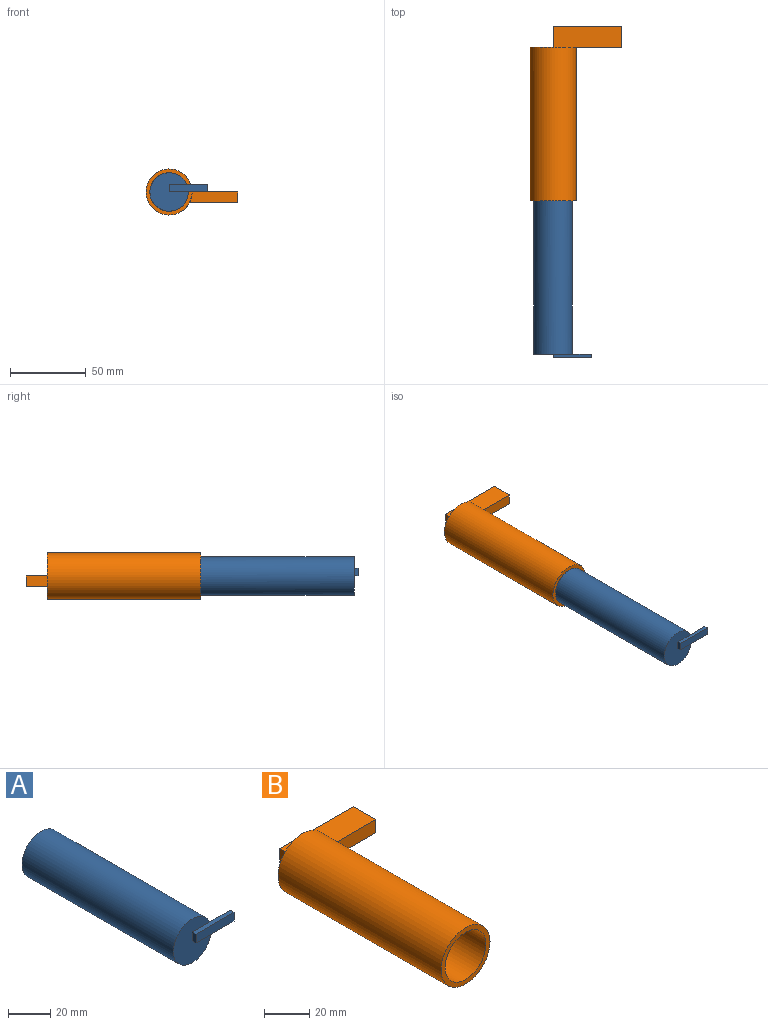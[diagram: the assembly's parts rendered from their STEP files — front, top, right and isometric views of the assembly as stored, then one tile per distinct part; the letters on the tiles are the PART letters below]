
ASSEMBLY  parts=2 mates=1
PART A: 9 faces, bbox 38.1x104.1x25.4 mm
  f0: plane 25.4x25.4mm, normal (0,-1,0), area 444mm2, adj f1,f4,f5,f6
  f1: cylinder r=12.7mm len=101.6mm, axis (0,1,0), area 8107.3mm2, adj f0,f2,f3
  f2: plane 25.4x25.4mm, normal (0,1,0), area 506.7mm2, adj f1
  f3: plane 13.76x5.08mm, normal (0,1,0), area 66.3mm2, adj f1,f4,f6,f7
  f4: plane 25.4x2.54mm, normal (0,0,1), area 64.5mm2, adj f0,f3,f5,f7,f8
  f5: plane 5.08x2.54mm, normal (-1,0,0), area 12.9mm2, adj f0,f4,f6,f8
  f6: plane 25.4x2.54mm, normal (0,0,-1), area 64.5mm2, adj f0,f3,f5,f7,f8
  f7: plane 5.08x2.54mm, normal (1,0,0), area 12.9mm2, adj f3,f4,f6,f8
  f8: plane 25.4x5.08mm, normal (0,-1,0), area 129mm2, adj f4,f5,f6,f7
PART B: 11 faces, bbox 60.8x115.6x30.5 mm
  f0: cylinder r=15.24mm len=101.6mm, axis (0,1,0), area 9728.8mm2, adj f1,f2,f9
  f1: plane 30.48x30.48mm, normal (0,-1,0), area 223mm2, adj f0,f3
  f2: plane 30.48x30.48mm, normal (0,1,0), area 624.7mm2, adj f0,f5,f6,f7
  f3: cylinder r=12.7mm len=99.06mm, axis (0,1,0), area 7904.6mm2, adj f1,f4
  f4: plane 25.4x25.4mm, normal (0,-1,0), area 506.7mm2, adj f3
  f5: plane 45.53x14mm, normal (0,0,-1), area 637.3mm2, adj f2,f6,f8,f9,f10
  f6: plane 14x7.16mm, normal (-1,0,0), area 100.2mm2, adj f2,f5,f7,f10
  f7: plane 45.53x14mm, normal (0,0,1), area 637.3mm2, adj f2,f6,f8,f9,f10
  f8: plane 14x7.16mm, normal (1,0,0), area 100.2mm2, adj f5,f7,f9,f10
  f9: plane 32.08x7.16mm, normal (0,-1,0), area 221.1mm2, adj f0,f5,f7,f8
  f10: plane 45.53x7.16mm, normal (0,1,0), area 326.1mm2, adj f5,f6,f7,f8
PLACE A t=(-75.2,-100.89,-12.63)mm
PLACE B t=(-75.2,0.71,-12.63)mm
MATE cylindrical A.f1 <-> B.f0  axis (0,1,0) through (-75.2,-100.89,-12.63)mm
